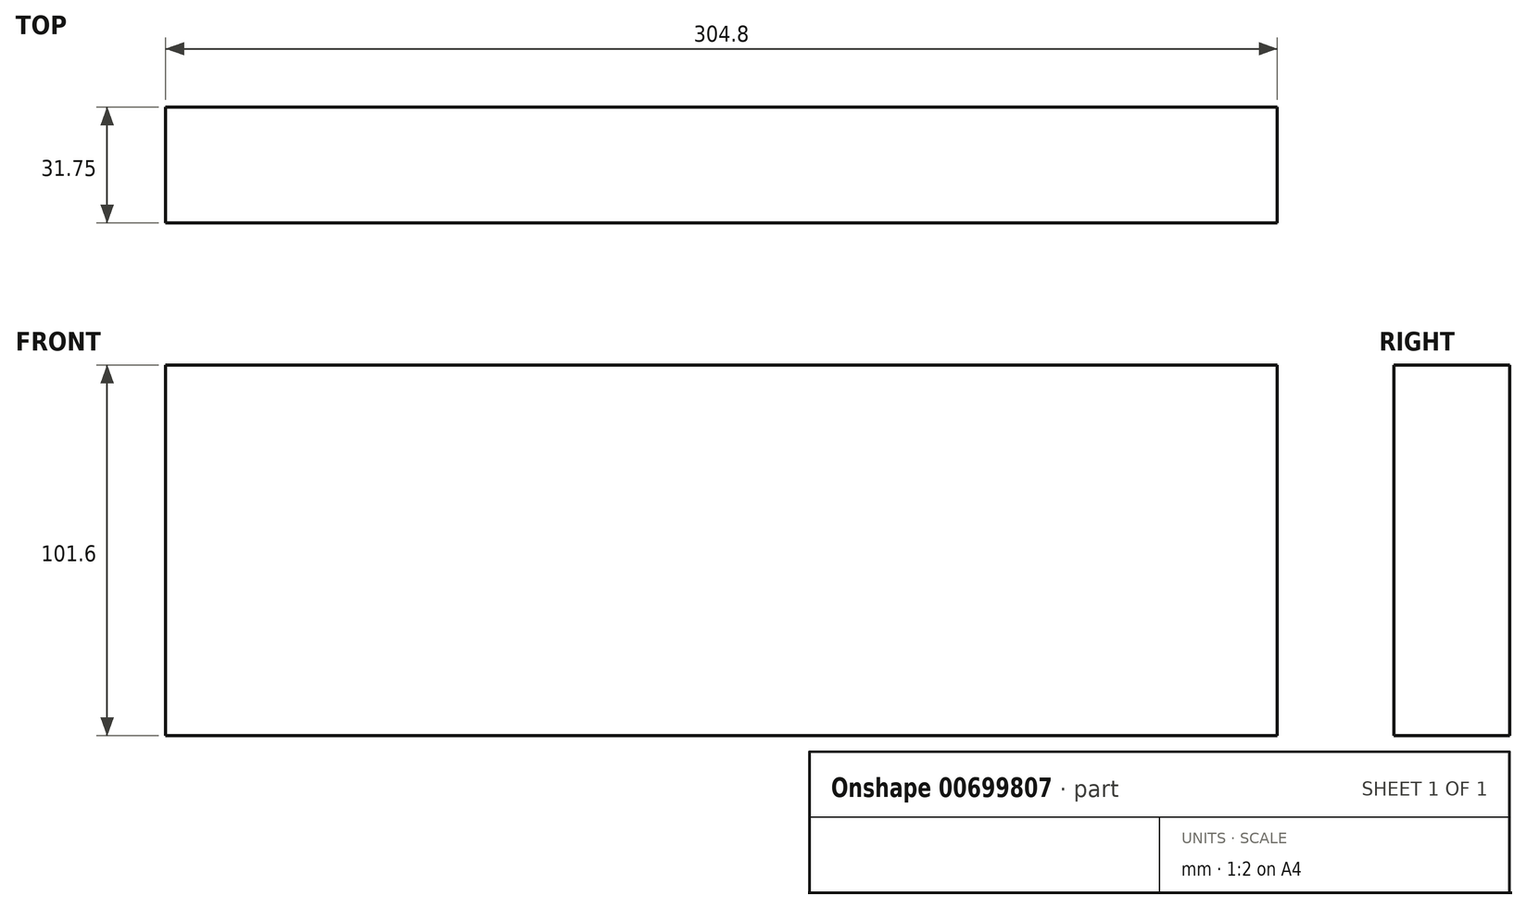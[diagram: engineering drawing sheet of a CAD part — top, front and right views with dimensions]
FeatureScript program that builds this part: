
annotation { "Feature Type Name" : "Feature", "Feature Type Description" : "" }
export const myFeature = defineFeature(function(context is Context, id is Id, definition is map)
    precondition{}
    {
        {
            var Q0;
            Q0=qCreatedBy(makeId("Front.planeOp"),FACE);
            var sketch = newSketch(context, id + "F0", { "sketchPlane" : qUnion([Q0])});
            skLineSegment(sketch, "E0.bottom", {"start": v(152.4, -50.8) * mm, "end": v(-152.4, -50.8) * mm});
            skLineSegment(sketch, "E0.top", {"start": v(152.4, 50.8) * mm, "end": v(-152.4, 50.8) * mm});
            skLineSegment(sketch, "E0.left", {"start": v(152.4, -50.8) * mm, "end": v(152.4, 50.8) * mm});
            skLineSegment(sketch, "E0.right", {"start": v(-152.4, -50.8) * mm, "end": v(-152.4, 50.8) * mm});
            skPoint(sketch, "E0.middle", {"position": v(0, 0) * mm});
            skSolve(sketch);
        }
        {
            var Q0;
            Q0=makeQuery(id+"F0.imprint","IMPRINT",FACE,{"disambiguationData":[TD([[makeQuery(id+"F0.imprint","IMPRINT",EDGE,{"derivedFrom":sQuery(id+"F0.wireOp",EDGE,"E0.bottom")}),-1.0]])]});
            extrude(context, id + "F1", {"entities" : qUnion([Q0]), "depth" : 31.75 * mm, "offsetDistance" : 25.4 * mm});
        }
    });
